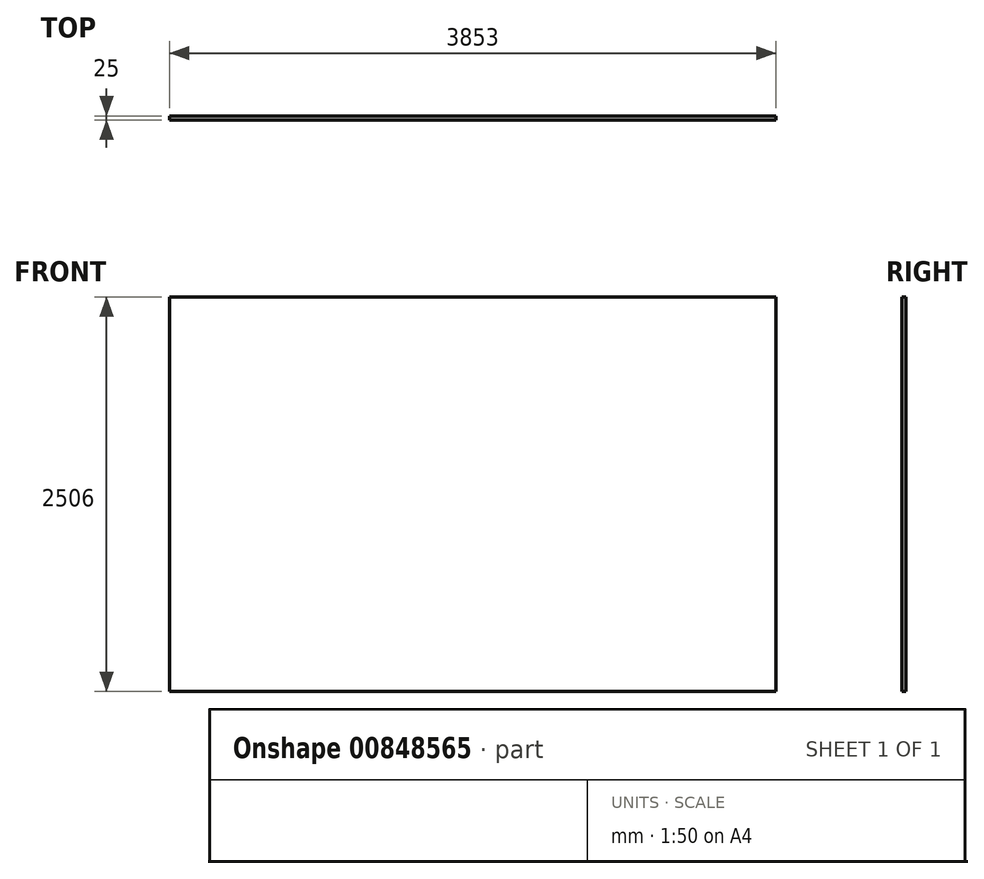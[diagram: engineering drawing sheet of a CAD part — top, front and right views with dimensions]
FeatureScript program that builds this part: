
annotation { "Feature Type Name" : "Feature", "Feature Type Description" : "" }
export const myFeature = defineFeature(function(context is Context, id is Id, definition is map)
    precondition{}
    {
        {
            var Q0;
            Q0=qCreatedBy(makeId("Front.planeOp"),FACE);
            var sketch = newSketch(context, id + "F0", { "sketchPlane" : qUnion([Q0])});
            skLineSegment(sketch, "E0.bottom", {"start": v(1926.5, 1253) * mm, "end": v(-1926.5, 1253) * mm});
            skLineSegment(sketch, "E0.top", {"start": v(1926.5, -1253) * mm, "end": v(-1926.5, -1253) * mm});
            skLineSegment(sketch, "E0.left", {"start": v(1926.5, 1253) * mm, "end": v(1926.5, -1253) * mm});
            skLineSegment(sketch, "E0.right", {"start": v(-1926.5, 1253) * mm, "end": v(-1926.5, -1253) * mm});
            skPoint(sketch, "E0.middle", {"position": v(0, 0) * mm});
            skSolve(sketch);
        }
        {
            var Q0;
            Q0 = qSketchRegion(id + "F0", true);
            extrude(context, id + "F1", {"entities" : qUnion([Q0]), "depth" : 25 * mm, "offsetDistance" : 25 * mm});
        }
    });
